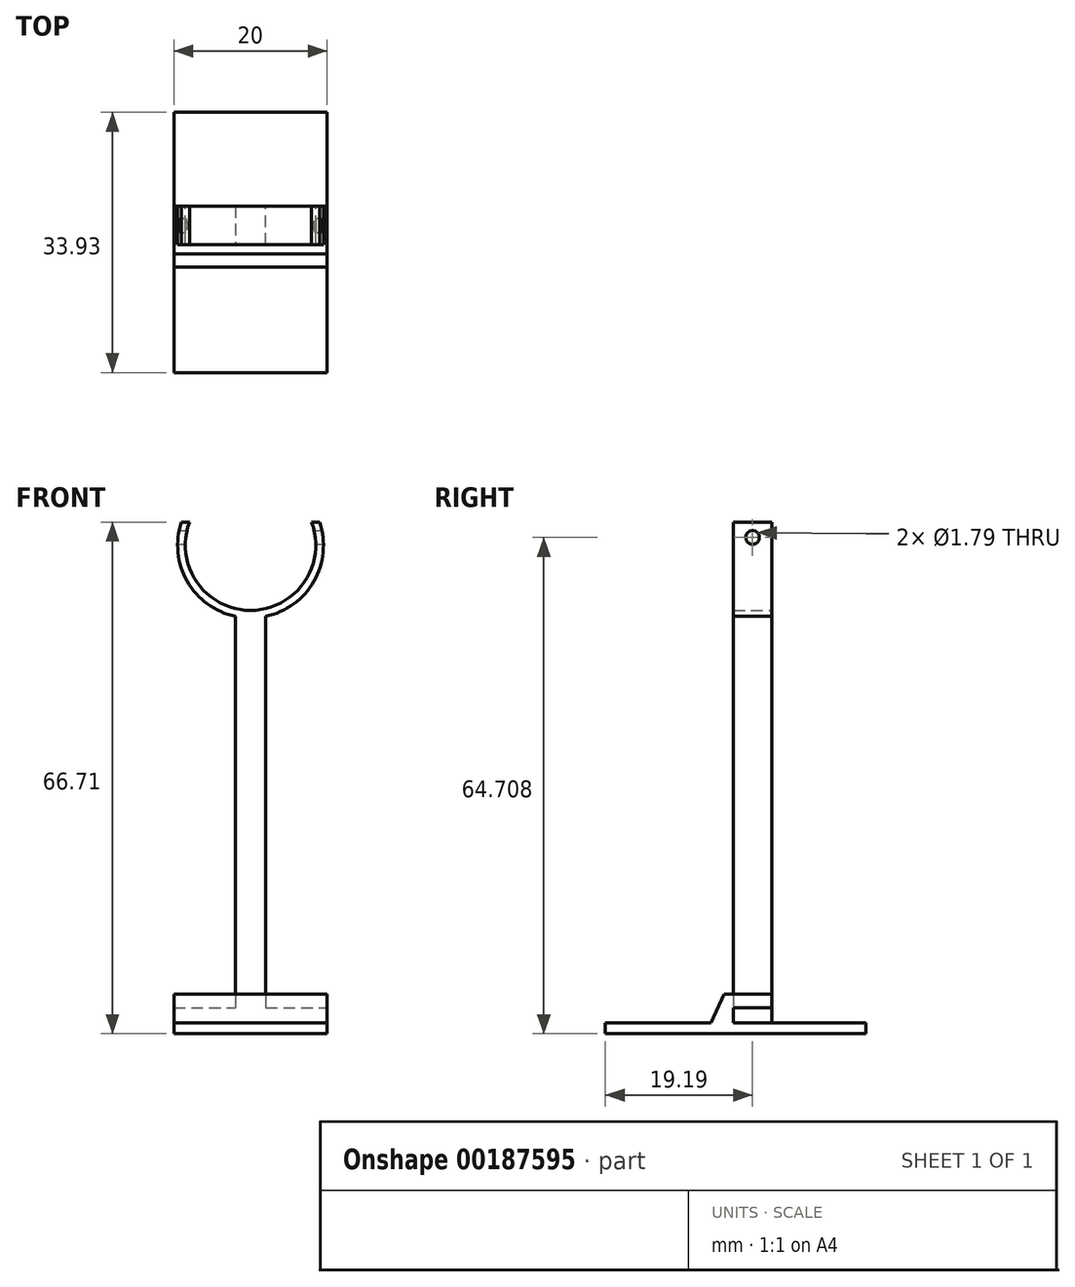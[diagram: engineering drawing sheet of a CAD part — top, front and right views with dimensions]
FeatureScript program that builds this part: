
annotation { "Feature Type Name" : "Feature", "Feature Type Description" : "" }
export const myFeature = defineFeature(function(context is Context, id is Id, definition is map)
    precondition{}
    {
        {
            var Q0;
            Q0=qCreatedBy(makeId("Front.planeOp"),FACE);
            var sketch = newSketch(context, id + "F0", { "sketchPlane" : qUnion([Q0])});
            skCircle(sketch, "E0", {"center": v(0, 54.03) * mm, "radius": 8.5 * mm});
            skCircle(sketch, "E1.0", {"center": v(0, 54.03) * mm, "radius": 9.5 * mm});
            skLineSegment(sketch, "E2", {"start": v(-2, 44.74) * mm, "end": v(-2, 36.74) * mm});
            skLineSegment(sketch, "E3", {"start": v(0, 69.97) * mm, "end": v(0, -72.68) * mm, "construction": true});
            skLineSegment(sketch, "E4.MirrorCS", {"start": v(2, 44.74) * mm, "end": v(2, 36.74) * mm});
            skLineSegment(sketch, "E5", {"start": v(-16.21, 54.03) * mm, "end": v(15.22, 54.03) * mm, "construction": true});
            skLineSegment(sketch, "E6", {"start": v(-9.01, 57.03) * mm, "end": v(9.01, 57.03) * mm});
            skLineSegment(sketch, "E7", {"start": v(-2, 36.74) * mm, "end": v(2, 36.74) * mm});
            skLineSegment(sketch, "E8", {"start": v(-2, 36.74) * mm, "end": v(-2, -8.26) * mm});
            skLineSegment(sketch, "E9", {"start": v(-2, -8.26) * mm, "end": v(2, -8.26) * mm});
            skLineSegment(sketch, "E10", {"start": v(2, -8.26) * mm, "end": v(2, 36.74) * mm});
            skPoint(sketch, "E11", {"position": v(0, -7.26) * mm});
            skLineSegment(sketch, "E12.bottom", {"start": v(10, -8.26) * mm, "end": v(-10, -8.26) * mm});
            skLineSegment(sketch, "E12.top", {"start": v(10, -6.26) * mm, "end": v(-10, -6.26) * mm});
            skLineSegment(sketch, "E12.left", {"start": v(10, -8.26) * mm, "end": v(10, -6.26) * mm});
            skLineSegment(sketch, "E12.right", {"start": v(-10, -8.26) * mm, "end": v(-10, -6.26) * mm});
            skSolve(sketch);
        }
        {
            var Q0;
            {var subQ0=sQuery(id+"F0.wireOp",EDGE,"E2");Q0=makeQuery(id+"F0.imprint","IMPRINT",FACE,{"disambiguationData":[TD([[makeQuery(id+"F0.imprint","IMPRINT",EDGE,{"derivedFrom":subQ0}),1.0]])]});}
            var Q1;
            {var subQ2=sQuery(id+"F0.wireOp",EDGE,"E6");var subQ6=sQuery(id+"F0.wireOp",EDGE,"E0");var subQ7=makeQuery(id+"F0.imprint","INTERSECT",VERTEX,{"disambiguationData":[OD(0.0)],"derivedFrom":[subQ6,subQ2]});Q1=makeQuery(id+"F0.imprint","IMPRINT",FACE,{"disambiguationData":[TD([[makeQuery(id+"F0.imprint","IMPRINT",EDGE,{"disambiguationData":[TD([[subQ7,-1.0]])],"derivedFrom":subQ6}),-1.0]])]});}
            var Q2;
            Q2=makeQuery(id+"F0.imprint","IMPRINT",FACE,{"disambiguationData":[TD([[makeQuery(id+"F0.imprint","IMPRINT",EDGE,{"derivedFrom":sQuery(id+"F0.wireOp",EDGE,"E7")}),-1.0]])]});
            var Q3;
            {var subQ5=sQuery(id+"F0.wireOp",EDGE,"E12.left");Q3=makeQuery(id+"F0.imprint","IMPRINT",FACE,{"disambiguationData":[TD([[makeQuery(id+"F0.imprint","IMPRINT",EDGE,{"derivedFrom":subQ5}),1.0]])]});}
            var Q4;
            {var subQ0=sQuery(id+"F0.wireOp",EDGE,"E12.bottom");var subQ1=sQuery(id+"F0.wireOp",EDGE,"E8");var subQ2=makeQuery(id+"F0.imprint","INTERSECT",VERTEX,{"derivedFrom":[subQ1,subQ0]});Q4=makeQuery(id+"F0.imprint","IMPRINT",FACE,{"disambiguationData":[TD([[makeQuery(id+"F0.imprint","IMPRINT",EDGE,{"disambiguationData":[TD([[subQ2,1.0]])],"derivedFrom":subQ1}),1.0]])]});}
            var Q5;
            {var subQ5=sQuery(id+"F0.wireOp",EDGE,"E12.right");Q5=makeQuery(id+"F0.imprint","IMPRINT",FACE,{"disambiguationData":[TD([[makeQuery(id+"F0.imprint","IMPRINT",EDGE,{"derivedFrom":subQ5}),-1.0]])]});}
            extrude(context, id + "F1", {"entities" : qUnion([Q0, Q1, Q2, Q3, Q4, Q5]), "depth" : 5 * mm});
        }
        {
            var Q0;
            Q0=makeQuery(id+"F1.opExtrude","SWEPT_FACE",FACE,{"disambiguationData":[OSD([sQuery(id+"F0.wireOp",EDGE,"E12.left")])]});
            var sketch = newSketch(context, id + "F2", { "sketchPlane" : qUnion([Q0])});
            skLineSegment(sketch, "E13.bottom", {"start": v(12.24, -6.26) * mm, "end": v(-21.7, -6.26) * mm});
            skLineSegment(sketch, "E13.top", {"start": v(12.24, -8.26) * mm, "end": v(-21.7, -8.26) * mm});
            skLineSegment(sketch, "E13.left", {"start": v(12.24, -6.26) * mm, "end": v(12.24, -8.26) * mm});
            skLineSegment(sketch, "E13.right", {"start": v(-21.7, -6.26) * mm, "end": v(-21.7, -8.26) * mm});
            skLineSegment(sketch, "E14.bottom", {"start": v(-21.7, -8.26) * mm, "end": v(12.24, -8.26) * mm});
            skLineSegment(sketch, "E14.top", {"start": v(-21.7, -9.68) * mm, "end": v(12.24, -9.68) * mm});
            skLineSegment(sketch, "E14.left", {"start": v(-21.7, -8.26) * mm, "end": v(-21.7, -9.68) * mm});
            skLineSegment(sketch, "E14.right", {"start": v(12.24, -8.26) * mm, "end": v(12.24, -9.68) * mm});
            skLineSegment(sketch, "E15", {"start": v(-7.92, -8.26) * mm, "end": v(-6.19, -4.53) * mm});
            skLineSegment(sketch, "E16", {"start": v(-6.19, -4.53) * mm, "end": v(0, -4.53) * mm});
            skLineSegment(sketch, "E17", {"start": v(0, -4.53) * mm, "end": v(0, -8.26) * mm});
            skSolve(sketch);
        }
        {
            var Q0;
            Q0=makeQuery(id+"F2.imprint","IMPRINT",FACE,{"disambiguationData":[TD([[makeQuery(id+"F2.imprint","IMPRINT",EDGE,{"derivedFrom":sQuery(id+"F2.wireOp",EDGE,"E14.top")}),1.0]])]});
            var Q1;
            {var subQ1=makeQuery(id+"F1.opExtrude","CAP_EDGE",EDGE,{"disambiguationData":[OSD([sQuery(id+"F0.wireOp",EDGE,"E12.left")])],"isStart":false});Q1=makeQuery(id+"F2.imprint","IMPRINT",FACE,{"disambiguationData":[TD([[makeQuery(id+"F2.imprint","IMPRINT",EDGE,{"derivedFrom":subQ1}),1.0]])]});}
            var Q2;
            {var subQ0=sQuery(id+"F2.wireOp",EDGE,"E16");Q2=makeQuery(id+"F2.imprint","IMPRINT",FACE,{"disambiguationData":[TD([[makeQuery(id+"F2.imprint","IMPRINT",EDGE,{"derivedFrom":subQ0}),-1.0]])]});}
            extrude(context, id + "F3", {"entities" : qUnion([Q0, Q1, Q2]), "oppositeDirection" : true, "depth" : 20 * mm});
        }
        {
            var Q0;
            Q0=makeQuery(id+"F1.opExtrude","SWEPT_BODY",BODY,{"disambiguationData":[OSD([sQuery(id+"F0.wireOp",EDGE,"E0"),sQuery(id+"F0.wireOp",EDGE,"E1.0"),sQuery(id+"F0.wireOp",EDGE,"E2"),sQuery(id+"F0.wireOp",EDGE,"E4.MirrorCS"),sQuery(id+"F0.wireOp",EDGE,"E6"),sQuery(id+"F0.wireOp",EDGE,"E8"),sQuery(id+"F0.wireOp",EDGE,"E10"),sQuery(id+"F0.wireOp",EDGE,"E12.bottom"),sQuery(id+"F0.wireOp",EDGE,"E12.top"),sQuery(id+"F0.wireOp",EDGE,"E12.left"),sQuery(id+"F0.wireOp",EDGE,"E12.right")])]});
            var Q1;
            Q1=makeQuery(id+"F3.opExtrude","SWEPT_BODY",BODY,{"disambiguationData":[OSD([sQuery(id+"F0.wireOp",EDGE,"E12.left"),sQuery(id+"F2.wireOp",EDGE,"E13.bottom"),sQuery(id+"F2.wireOp",EDGE,"E14.bottom"),sQuery(id+"F2.wireOp",EDGE,"E14.top"),sQuery(id+"F2.wireOp",EDGE,"E14.left"),sQuery(id+"F2.wireOp",EDGE,"E14.right"),sQuery(id+"F2.wireOp",EDGE,"E15"),sQuery(id+"F2.wireOp",EDGE,"E16"),sQuery(id+"F2.wireOp",EDGE,"E17")])]});
            booleanBodies(context, id + "F4", {"operationType" : BooleanOperationType.SUBTRACTION, "tools" : qUnion([Q0]), "targets" : qUnion([Q1]), "keepTools" : true});
        }
        {
            var Q0;
            Q0=qCreatedBy(makeId("Right.planeOp"),FACE);
            var sketch = newSketch(context, id + "F5", { "sketchPlane" : qUnion([Q0])});
            skLineSegment(sketch, "E18.0", {"start": v(-5, 57.03) * mm, "end": v(0, 57.03) * mm});
            skLineSegment(sketch, "E19", {"start": v(-2.5, 57.03) * mm, "end": v(-2.5, 51.36) * mm, "construction": true});
            skCircle(sketch, "E20", {"center": v(-2.5, 55.03) * mm, "radius": 0.9 * mm});
            skSolve(sketch);
        }
        {
            var Q0;
            Q0=makeQuery(id+"F5.imprint","IMPRINT",FACE,{"disambiguationData":[TD([[makeQuery(id+"F5.imprint","IMPRINT",EDGE,{"derivedFrom":sQuery(id+"F5.wireOp",EDGE,"E20")}),1.0]])]});
            extrude(context, id + "F6", {"entities" : qUnion([Q0]), "operationType" : NewBodyOperationType.REMOVE, "endBound" : BoundingType.SYMMETRIC, "oppositeDirection" : true, "depth" : 25 * mm});
        }
    });
